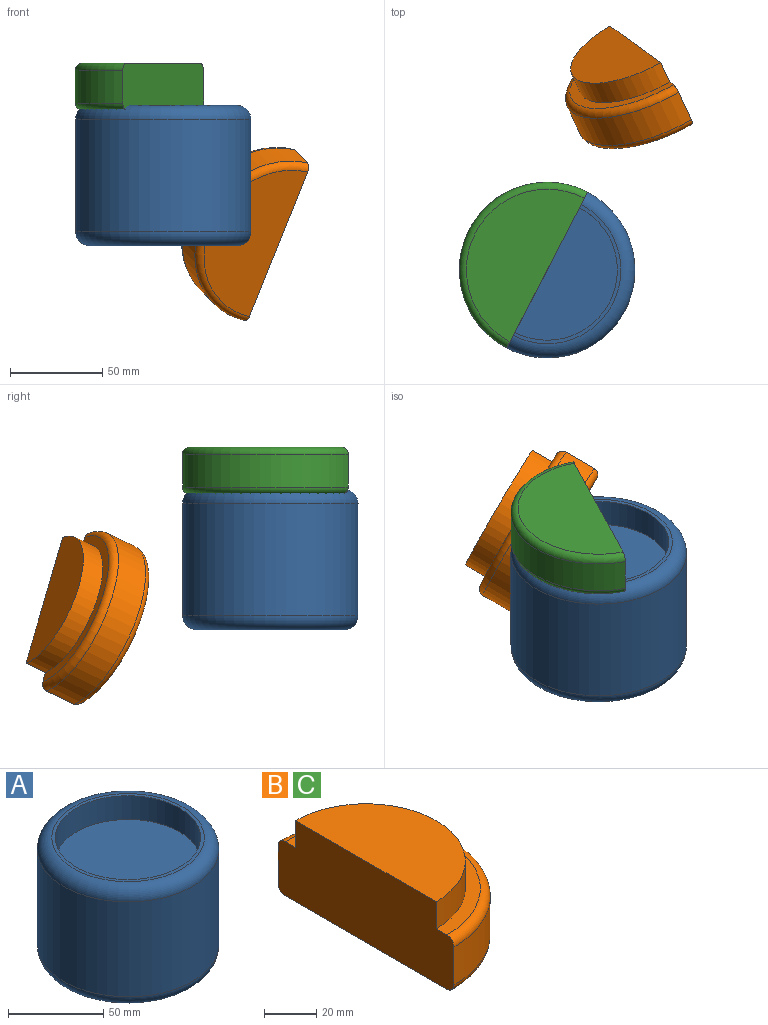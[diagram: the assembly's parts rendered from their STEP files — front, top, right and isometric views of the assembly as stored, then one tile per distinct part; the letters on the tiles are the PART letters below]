
ASSEMBLY  parts=3 mates=1
PART A: 7 faces, bbox 103.1x103.1x76.2 mm
  f0: cylinder r=47.62mm len=95.25mm, axis (0,0,-1), area 18241.5mm2, adj f4,f5
  f1: plane 80.01x80.01mm, normal (0,0,1), area 467.4mm2, adj f3,f4
  f2: plane 80.01x80.01mm, normal (0,0,-1), area 5027.8mm2, adj f5
  f3: cylinder r=38.1mm len=76.2mm, axis (0,0,1), area 3648.3mm2, adj f1,f6
  f4: torus R=40mm, axis (0,0,1), area 3373.5mm2, adj f0,f1
  f5: torus R=40mm, axis (0,0,1), area 3373.5mm2, adj f0,f2
  f6: plane 76.2x76.2mm, normal (0,0,1), area 4560.4mm2, adj f3
PART B: 8 faces, bbox 51.5x103.1x38.1 mm
  f0: torus R=43.81mm, axis (0,0,1), area 869.4mm2, adj f1,f6,f7
  f1: plane 87.63x43.82mm, normal (0,0,-1), area 3015.5mm2, adj f0,f7
  f2: plane 76.2x38.1mm, normal (0,0,1), area 2280.2mm2, adj f3,f7
  f3: cylinder r=38.1mm len=76.2mm, axis (0,0,-1), area 1520.1mm2, adj f2,f5,f7
  f4: torus R=43.81mm, axis (0,0,1), area 869.4mm2, adj f5,f6,f7
  f5: plane 87.63x43.82mm, normal (0,0,1), area 735.4mm2, adj f3,f4,f7
  f6: cylinder r=47.62mm len=95.25mm, axis (0,0,-1), area 2660.2mm2, adj f0,f4,f7
  f7: plane 95.25x38.1mm, normal (-1,0,0), area 3374.6mm2, adj f0,f1,f2,f3,f4,f5,f6
PART C: same geometry as B
PLACE A rot(axis=(0.88,-0.05,-0.46),0deg) t=(-47.8,-122.6,-15.98)mm fixed
PLACE B rot(axis=(0.06,-0.57,-0.82),148.8deg) t=(14.77,-31.67,-15.19)mm
PLACE C rot(axis=(-0.24,-0.97,0),180deg) t=(-47.8,-122.6,83.08)mm
MATE revolute A.f0 <-> C.f0  axis (0,0,1) through (-47.8,-122.6,44.98)mm
